# Revit family: G6 PL+ MS650919PM
name_source: partatom
category: Datengeräte
units: mm (PartAtom-declared; Revit-internal decimal feet)

## family parameters
Arbeitsebenenbasiert = Nein
Beim Laden mit Abzugskörper schneiden = Nein
Bemaßung runder Anschluss = Durchmesser verwenden
Beschriftungsausrichtung beibehalten = Nein
Gemeinsam genutzt = Nein
Immer vertikal = Ja
OmniClass-Nummer = 23.85.50.17
OmniClass-Titel = Communication and Data Processing Equipment
Raumberechnungspunkt = Nein
Teiletyp = Normal

## types (2) — shared parameters
Artikelnummer = MS650919PM
Beschreibung = 7 Port GBE Industrial PLR+ Switch PoE+
Hersteller = MICROSENS
Interface 1 = 2 x 100/1000X SFP-Slots / 10/100/1000T (Combo)
Interface 10 = RS-232 Port (RJ-45)
Interface 2 = 5 x 10/100/1000T
Interface 3 = 4 x PoE+
Interface 4 = 1 x PD
Interface 5 = 2 x 24..57VDC
Interface 6 = DIN-Rail
Interface 7 = USB
Interface 9 = 2 x I/O
zero-valued in all types: Vorgabe-Ansicht

## per-type parameters (varying)
| type | Interface 8 | Property 1 |
| MS652119PM-V2 | SD-Karte inkl. | Managed |
| MS650919PM | SD-Card incl. | Managed switch |
